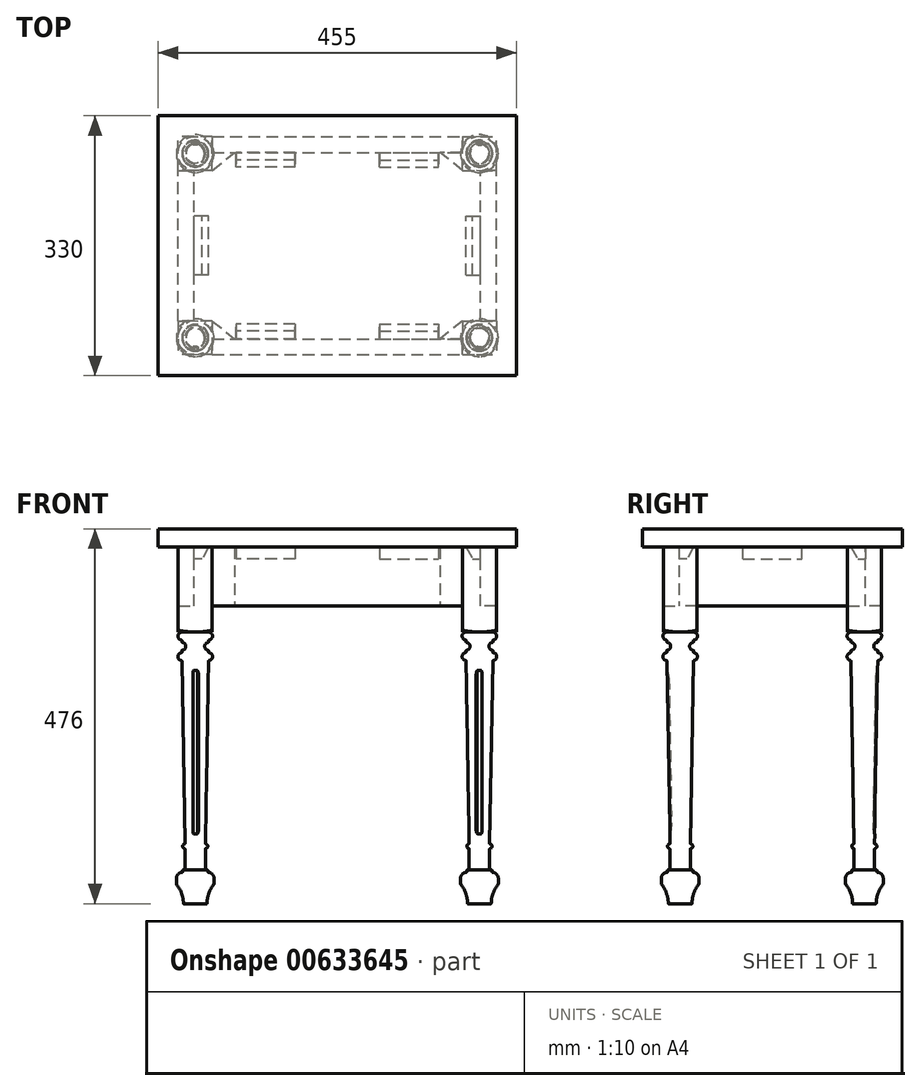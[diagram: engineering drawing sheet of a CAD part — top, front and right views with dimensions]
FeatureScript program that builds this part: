
annotation { "Feature Type Name" : "Feature", "Feature Type Description" : "" }
export const myFeature = defineFeature(function(context is Context, id is Id, definition is map)
    precondition{}
    {
        {
            var Q0;
            Q0=qCreatedBy(makeId("Top.planeOp"),FACE);
            var sketch = newSketch(context, id + "F0", { "sketchPlane" : qUnion([Q0])});
            skLineSegment(sketch, "E0.bottom", {"start": v(-227.5, -165) * mm, "end": v(227.5, -165) * mm});
            skLineSegment(sketch, "E0.top", {"start": v(-227.5, 165) * mm, "end": v(227.5, 165) * mm});
            skLineSegment(sketch, "E0.left", {"start": v(-227.5, -165) * mm, "end": v(-227.5, 165) * mm});
            skLineSegment(sketch, "E0.right", {"start": v(227.5, -165) * mm, "end": v(227.5, 165) * mm});
            skPoint(sketch, "E0.middle", {"position": v(0, 0) * mm});
            skSolve(sketch);
        }
        {
            var Q0;
            Q0 = qSketchRegion(id + "F0", true);
            extrude(context, id + "F1", {"entities" : qUnion([Q0]), "oppositeDirection" : true, "depth" : 23 * mm, "offsetDistance" : 25 * mm});
        }
        {
            var Q0;
            Q0=makeQuery(id+"F1.opExtrude","CAP_FACE",FACE,{"disambiguationData":[OSD([sQuery(id+"F0.wireOp",EDGE,"E0.bottom"),sQuery(id+"F0.wireOp",EDGE,"E0.top"),sQuery(id+"F0.wireOp",EDGE,"E0.left"),sQuery(id+"F0.wireOp",EDGE,"E0.right")])],"isStart":false});
            var sketch = newSketch(context, id + "F2", { "sketchPlane" : qUnion([Q0])});
            skLineSegment(sketch, "E1.bottom", {"start": v(-159, 95.5) * mm, "end": v(-202, 95.5) * mm});
            skLineSegment(sketch, "E1.top", {"start": v(-159, 138.5) * mm, "end": v(-202, 138.5) * mm});
            skLineSegment(sketch, "E1.left", {"start": v(-159, 95.5) * mm, "end": v(-159, 138.5) * mm});
            skLineSegment(sketch, "E1.right", {"start": v(-202, 95.5) * mm, "end": v(-202, 138.5) * mm});
            skPoint(sketch, "E1.middle", {"position": v(-180.5, 117) * mm});
            skSolve(sketch);
        }
        {
            var Q0;
            Q0 = qSketchRegion(id + "F2", true);
            extrude(context, id + "F3", {"entities" : qUnion([Q0]), "depth" : 108 * mm, "offsetDistance" : 25 * mm});
        }
        {
            var Q0;
            Q0=makeQuery(id+"F3.opExtrude","SWEPT_FACE",FACE,{"disambiguationData":[OSD([sQuery(id+"F2.wireOp",EDGE,"E1.right")])]});
            var Q1;
            Q1=makeQuery(id+"F3.opExtrude","SWEPT_FACE",FACE,{"disambiguationData":[OSD([sQuery(id+"F2.wireOp",EDGE,"E1.left")])]});
            cPlane(context, id + "F4", {"entities" : qUnion([Q0, Q1]), "cplaneType" : CPlaneType.MID_PLANE, "offset" : 25 * mm, "width" : 150 * mm, "height" : 150 * mm});
        }
        {
            var Q0;
            Q0=qCreatedBy(id+"F4.planeOp",FACE);
            var sketch = newSketch(context, id + "F5", { "sketchPlane" : qUnion([Q0])});
            skLineSegment(sketch, "E2.0", {"start": v(117, -131) * mm, "end": v(134, -131) * mm});
            skLineSegment(sketch, "E3", {"start": v(117, -131) * mm, "end": v(117, -476) * mm});
            skLineSegment(sketch, "E4", {"start": v(117, -476) * mm, "end": v(132, -476) * mm});
            skArc(sketch, "E5", {"start": v(141, -451) * mm, "mid": v(134.32, -462.71) * mm, "end": v(132, -476) * mm});
            skArc(sketch, "E6", {"start": v(130, -406) * mm, "mid": v(133, -403) * mm, "end": v(130, -400) * mm});
            skLineSegment(sketch, "E7", {"start": v(130, -400) * mm, "end": v(134, -167) * mm});
            skArc(sketch, "E8", {"start": v(134, -167) * mm, "mid": v(139, -162) * mm, "end": v(134, -157) * mm});
            skLineSegment(sketch, "E9", {"start": v(134, -157) * mm, "end": v(134, -154) * mm});
            skArc(sketch, "E10", {"start": v(134, -144) * mm, "mid": v(129, -149) * mm, "end": v(134, -154) * mm});
            skLineSegment(sketch, "E11", {"start": v(134, -144) * mm, "end": v(134, -141) * mm});
            skArc(sketch, "E12", {"start": v(134, -141) * mm, "mid": v(139, -136) * mm, "end": v(134, -131) * mm});
            skLineSegment(sketch, "E13", {"start": v(130, -406) * mm, "end": v(130, -433) * mm});
            skLineSegment(sketch, "E14", {"start": v(130, -433) * mm, "end": v(133, -433) * mm});
            skLineSegment(sketch, "E15", {"start": v(133, -433) * mm, "end": v(133, -436) * mm});
            skLineSegment(sketch, "E16", {"start": v(141, -436) * mm, "end": v(141, -451) * mm});
            skPoint(sketch, "E17.orphan", {"position": v(138.5, -131) * mm});
            skPoint(sketch, "E18.orphan", {"position": v(95.5, -131) * mm});
            skLineSegment(sketch, "E19", {"start": v(133, -436) * mm, "end": v(141, -436) * mm});
            skSolve(sketch);
        }
        {
            var Q0;
            Q0=makeQuery(id+"F5.imprint","IMPRINT",FACE,{"disambiguationData":[TD([[makeQuery(id+"F5.imprint","IMPRINT",EDGE,{"derivedFrom":sQuery(id+"F5.wireOp",EDGE,"E2.0")}),-1.0]])]});
            var Q1;
            Q1=sQuery(id+"F5.wireOp",EDGE,"E3");
            revolve(context, id + "F6", {"operationType" : NewBodyOperationType.ADD, "entities" : qUnion([Q0]), "axis" : qUnion([Q1]), "revolveType" : RevolveType.FULL});
        }
        {
            var Q0;
            Q0=makeQuery(id+"F6.opRevolve","SWEPT_EDGE",EDGE,{"disambiguationData":[OSD([sQuery(id+"F5.wireOp",EDGE,"E16"),sQuery(id+"F5.wireOp",EDGE,"E19")])]});
            fillet(context, id + "F7", {"entities" : qUnion([Q0]), "radius" : 8 * mm, "tangentPropagation" : true, "allowEdgeOverflow" : false});
        }
        {
            var Q0;
            Q0=makeQuery(id+"F6.opRevolve","SWEPT_EDGE",EDGE,{"disambiguationData":[OSD([sQuery(id+"F5.wireOp",EDGE,"E13"),sQuery(id+"F5.wireOp",EDGE,"E14")])]});
            var Q1;
            Q1=makeQuery(id+"F6.opRevolve","SWEPT_EDGE",EDGE,{"disambiguationData":[OSD([sQuery(id+"F5.wireOp",EDGE,"E5"),sQuery(id+"F5.wireOp",EDGE,"E16")])]});
            fillet(context, id + "F8", {"entities" : qUnion([Q0, Q1]), "radius" : 2.5 * mm, "tangentPropagation" : true, "allowEdgeOverflow" : false});
        }
        {
            var Q0;
            Q0=makeQuery(id+"F6.opRevolve","SWEPT_EDGE",EDGE,{"disambiguationData":[OSD([sQuery(id+"F5.wireOp",EDGE,"E14"),sQuery(id+"F5.wireOp",EDGE,"E15")])]});
            var Q1;
            Q1=makeQuery(id+"F7.opFillet","BLEND_EDGE",EDGE,{"blendedFrom":[makeQuery(id+"F6.opRevolve","SWEPT_EDGE",EDGE,{"disambiguationData":[OSD([sQuery(id+"F5.wireOp",EDGE,"E16"),sQuery(id+"F5.wireOp",EDGE,"E19")])]}),makeQuery(id+"F6.opRevolve","SWEPT_FACE",FACE,{"disambiguationData":[OSD([sQuery(id+"F5.wireOp",EDGE,"E15")])]})],"blendedInto":[makeQuery(id+"F6.opRevolve","SWEPT_FACE",FACE,{"disambiguationData":[OSD([sQuery(id+"F5.wireOp",EDGE,"E15")])]})]});
            var Q2;
            Q2=makeQuery(id+"F6.opRevolve","SWEPT_EDGE",EDGE,{"disambiguationData":[OSD([sQuery(id+"F5.wireOp",EDGE,"E6"),sQuery(id+"F5.wireOp",EDGE,"E7")])]});
            var Q3;
            Q3=makeQuery(id+"F6.opRevolve","SWEPT_EDGE",EDGE,{"disambiguationData":[OSD([sQuery(id+"F5.wireOp",EDGE,"E6"),sQuery(id+"F5.wireOp",EDGE,"E13")])]});
            var Q4;
            Q4=makeQuery(id+"F6.opRevolve","SWEPT_EDGE",EDGE,{"disambiguationData":[OSD([sQuery(id+"F5.wireOp",EDGE,"E11"),sQuery(id+"F5.wireOp",EDGE,"E12")])]});
            var Q5;
            Q5=makeQuery(id+"F6.opRevolve","SWEPT_EDGE",EDGE,{"disambiguationData":[OSD([sQuery(id+"F5.wireOp",EDGE,"E10"),sQuery(id+"F5.wireOp",EDGE,"E11")])]});
            var Q6;
            Q6=makeQuery(id+"F6.opRevolve","SWEPT_EDGE",EDGE,{"disambiguationData":[OSD([sQuery(id+"F5.wireOp",EDGE,"E9"),sQuery(id+"F5.wireOp",EDGE,"E10")])]});
            var Q7;
            Q7=makeQuery(id+"F6.opRevolve","SWEPT_EDGE",EDGE,{"disambiguationData":[OSD([sQuery(id+"F5.wireOp",EDGE,"E8"),sQuery(id+"F5.wireOp",EDGE,"E9")])]});
            var Q8;
            Q8=makeQuery(id+"F6.opRevolve","SWEPT_EDGE",EDGE,{"disambiguationData":[OSD([sQuery(id+"F5.wireOp",EDGE,"E7"),sQuery(id+"F5.wireOp",EDGE,"E8")])]});
            var Q9;
            Q9=makeQuery(id+"F6.opRevolve","SWEPT_EDGE",EDGE,{"disambiguationData":[OSD([sQuery(id+"F5.wireOp",EDGE,"E4"),sQuery(id+"F5.wireOp",EDGE,"E5")])]});
            fillet(context, id + "F9", {"entities" : qUnion([Q0, Q1, Q2, Q3, Q4, Q5, Q6, Q7, Q8, Q9]), "radius" : .5 * mm, "tangentPropagation" : true, "allowEdgeOverflow" : false});
        }
        {
            var Q0;
            Q0=makeQuery(id+"F3.opExtrude","SWEPT_EDGE",EDGE,{"disambiguationData":[OSD([sQuery(id+"F2.wireOp",EDGE,"E1.top"),sQuery(id+"F2.wireOp",EDGE,"E1.right")])]});
            var Q1;
            Q1=makeQuery(id+"F3.opExtrude","SWEPT_EDGE",EDGE,{"disambiguationData":[OSD([sQuery(id+"F2.wireOp",EDGE,"E1.bottom"),sQuery(id+"F2.wireOp",EDGE,"E1.left")])]});
            cPlane(context, id + "F10", {"entities" : qUnion([Q0, Q1]), "cplaneType" : CPlaneType.LINE_ANGLE, "offset" : 25 * mm, "angle" : 0 * degree, "width" : 150 * mm, "height" : 150 * mm});
        }
        {
            var Q0;
            Q0=qCreatedBy(id+"F10.planeOp",FACE);
            var sketch = newSketch(context, id + "F11", { "sketchPlane" : qUnion([Q0])});
            skLineSegment(sketch, "E20.0", {"start": v(210.36, -131) * mm, "end": v(210.36, -23) * mm});
            skArc(sketch, "E21", {"start": v(179.69, -128) * mm, "mid": v(186.03, -130.24) * mm, "end": v(192.72, -131) * mm});
            skLineSegment(sketch, "E22", {"start": v(179.69, -128) * mm, "end": v(179.69, -131) * mm});
            skLineSegment(sketch, "E23", {"start": v(179.69, -131) * mm, "end": v(192.72, -131) * mm});
            skSolve(sketch);
        }
        {
            var Q0;
            Q0=makeQuery(id+"F11.imprint","IMPRINT",FACE,{"disambiguationData":[TD([[makeQuery(id+"F11.imprint","IMPRINT",EDGE,{"derivedFrom":sQuery(id+"F11.wireOp",EDGE,"E21")}),-1.0]])]});
            var Q1;
            Q1=sQuery(id+"F11.wireOp",EDGE,"E20.0");
            revolve(context, id + "F12", {"operationType" : NewBodyOperationType.REMOVE, "entities" : qUnion([Q0]), "axis" : qUnion([Q1]), "revolveType" : RevolveType.FULL, "oppositeDirection" : true});
        }
        {
            var Q0;
            Q0=qCreatedBy(id+"F4.planeOp",FACE);
            var sketch = newSketch(context, id + "F13", { "sketchPlane" : qUnion([Q0])});
            skLineSegment(sketch, "E24.0", {"start": v(134, -167.47) * mm, "end": v(100, -167.47) * mm});
            skLineSegment(sketch, "E25.0", {"start": v(104, -399.53) * mm, "end": v(130, -399.53) * mm});
            skLineSegment(sketch, "E26", {"start": v(117, -399.53) * mm, "end": v(117, -167.47) * mm});
            skLineSegment(sketch, "E27", {"start": v(134.02, -165.87) * mm, "end": v(130.21, -387.53) * mm});
            skLineSegment(sketch, "E28", {"start": v(131.12, -189.1) * mm, "end": v(127.88, -377.8) * mm});
            skArc(sketch, "E29", {"start": v(133.79, -179.47) * mm, "mid": v(131.84, -184.12) * mm, "end": v(131.12, -189.1) * mm});
            skArc(sketch, "E30", {"start": v(127.88, -377.8) * mm, "mid": v(128.43, -382.81) * mm, "end": v(130.21, -387.53) * mm});
            skLineSegment(sketch, "E31", {"start": v(147.88, -378.15) * mm, "end": v(151.12, -189.45) * mm, "construction": true});
            skSolve(sketch);
        }
        {
            var Q0;
            Q0=makeQuery(id+"F13.imprint","IMPRINT",FACE,{"disambiguationData":[TD([[makeQuery(id+"F13.imprint","IMPRINT",EDGE,{"derivedFrom":sQuery(id+"F13.wireOp",EDGE,"E28")}),1.0]])]});
            extrude(context, id + "F14", {"entities" : qUnion([Q0]), "operationType" : NewBodyOperationType.REMOVE, "endBound" : BoundingType.SYMMETRIC, "oppositeDirection" : true, "depth" : 6 * mm, "offsetDistance" : 25 * mm});
        }
        {
            var Q0;
            Q0=makeQuery(id+"F14.boolean.opBoolean","COPY",EDGE,{"derivedFrom":makeQuery(id+"F14.opExtrude","CAP_EDGE",EDGE,{"disambiguationData":[OSD([sQuery(id+"F13.wireOp",EDGE,"E28")])],"isStart":false})});
            var Q1;
            Q1=makeQuery(id+"F14.boolean.opBoolean","COPY",EDGE,{"derivedFrom":makeQuery(id+"F14.opExtrude","CAP_EDGE",EDGE,{"disambiguationData":[OSD([sQuery(id+"F13.wireOp",EDGE,"E28")])],"isStart":true})});
            var Q2;
            Q2=makeQuery(id+"F14.boolean.opBoolean","INTERSECT",EDGE,{"derivedFrom":[makeQuery(id+"F6.opRevolve","SWEPT_FACE",FACE,{"disambiguationData":[OSD([sQuery(id+"F5.wireOp",EDGE,"E7")])]}),makeQuery(id+"F14.opExtrude","CAP_FACE",FACE,{"disambiguationData":[OSD([sQuery(id+"F13.wireOp",EDGE,"E27"),sQuery(id+"F13.wireOp",EDGE,"E28"),sQuery(id+"F13.wireOp",EDGE,"E29"),sQuery(id+"F13.wireOp",EDGE,"E30")])],"isStart":false})]});
            fillet(context, id + "F15", {"entities" : qUnion([Q0, Q1, Q2]), "radius" : .9 * mm, "tangentPropagation" : true, "allowEdgeOverflow" : false});
        }
        {
            var Q0;
            Q0=makeQuery(id+"F3.opExtrude","SWEPT_BODY",BODY,{"disambiguationData":[OSD([sQuery(id+"F2.wireOp",EDGE,"E1.bottom"),sQuery(id+"F2.wireOp",EDGE,"E1.top"),sQuery(id+"F2.wireOp",EDGE,"E1.left"),sQuery(id+"F2.wireOp",EDGE,"E1.right")])]});
            var Q1;
            Q1=qCreatedBy(makeId("Right.planeOp"),FACE);
            mirror(context, id + "F16", {"entities" : qUnion([Q0]), "mirrorPlane" : qUnion([Q1])});
        }
        {
            var Q0;
            Q0=makeQuery(id+"F1.opExtrude","CAP_FACE",FACE,{"disambiguationData":[OSD([sQuery(id+"F0.wireOp",EDGE,"E0.bottom"),sQuery(id+"F0.wireOp",EDGE,"E0.top"),sQuery(id+"F0.wireOp",EDGE,"E0.left"),sQuery(id+"F0.wireOp",EDGE,"E0.right")])],"isStart":false});
            var sketch = newSketch(context, id + "F17", { "sketchPlane" : qUnion([Q0])});
            skPoint(sketch, "E32.0", {"position": v(-159, 138.5) * mm});
            skPoint(sketch, "E33.0", {"position": v(159, 138.5) * mm});
            skLineSegment(sketch, "E34.bottom", {"start": v(-159, 138.5) * mm, "end": v(159, 138.5) * mm});
            skLineSegment(sketch, "E34.top", {"start": v(-159, 118.5) * mm, "end": v(159, 118.5) * mm});
            skLineSegment(sketch, "E34.left", {"start": v(-159, 138.5) * mm, "end": v(-159, 118.5) * mm});
            skLineSegment(sketch, "E34.right", {"start": v(159, 138.5) * mm, "end": v(159, 118.5) * mm});
            skSolve(sketch);
        }
        {
            var Q0;
            Q0 = qSketchRegion(id + "F17", true);
            extrude(context, id + "F18", {"entities" : qUnion([Q0]), "depth" : 75 * mm, "offsetDistance" : 25 * mm});
        }
        {
            var Q0;
            Q0=makeQuery(id+"F3.opExtrude","SWEPT_BODY",BODY,{"disambiguationData":[OSD([sQuery(id+"F2.wireOp",EDGE,"E1.bottom"),sQuery(id+"F2.wireOp",EDGE,"E1.top"),sQuery(id+"F2.wireOp",EDGE,"E1.left"),sQuery(id+"F2.wireOp",EDGE,"E1.right")])]});
            var Q1;
            Q1=makeQuery(id+"F18.opExtrude","SWEPT_BODY",BODY,{"disambiguationData":[OSD([sQuery(id+"F17.wireOp",EDGE,"E34.bottom"),sQuery(id+"F17.wireOp",EDGE,"E34.top"),sQuery(id+"F17.wireOp",EDGE,"E34.left"),sQuery(id+"F17.wireOp",EDGE,"E34.right")])]});
            var Q2;
            Q2=makeQuery(id+"F16.opPattern","COPY",BODY,{"derivedFrom":makeQuery(id+"F3.opExtrude","SWEPT_BODY",BODY,{"disambiguationData":[OSD([sQuery(id+"F2.wireOp",EDGE,"E1.bottom"),sQuery(id+"F2.wireOp",EDGE,"E1.top"),sQuery(id+"F2.wireOp",EDGE,"E1.left"),sQuery(id+"F2.wireOp",EDGE,"E1.right")])]}),"instanceName":"1"});
            var Q3;
            Q3=qCreatedBy(makeId("Front.planeOp"),FACE);
            mirror(context, id + "F19", {"entities" : qUnion([Q0, Q1, Q2]), "mirrorPlane" : qUnion([Q3])});
        }
        {
            var Q0;
            Q0=makeQuery(id+"F1.opExtrude","CAP_FACE",FACE,{"disambiguationData":[OSD([sQuery(id+"F0.wireOp",EDGE,"E0.bottom"),sQuery(id+"F0.wireOp",EDGE,"E0.top"),sQuery(id+"F0.wireOp",EDGE,"E0.left"),sQuery(id+"F0.wireOp",EDGE,"E0.right")])],"isStart":false});
            var sketch = newSketch(context, id + "F20", { "sketchPlane" : qUnion([Q0])});
            skPoint(sketch, "E35.0", {"position": v(202, 95.5) * mm});
            skPoint(sketch, "E36.0", {"position": v(159, -95.5) * mm});
            skLineSegment(sketch, "E37.bottom", {"start": v(202, 95.5) * mm, "end": v(182, 95.5) * mm});
            skLineSegment(sketch, "E37.top", {"start": v(202, -95.5) * mm, "end": v(182, -95.5) * mm});
            skLineSegment(sketch, "E37.left", {"start": v(202, 95.5) * mm, "end": v(202, -95.5) * mm});
            skLineSegment(sketch, "E37.right", {"start": v(182, 95.5) * mm, "end": v(182, -95.5) * mm});
            skSolve(sketch);
        }
        {
            var Q0;
            Q0 = qSketchRegion(id + "F20", true);
            var Q1;
            Q1=makeQuery(id+"F19.opPattern","COPY",FACE,{"derivedFrom":makeQuery(id+"F18.opExtrude","CAP_FACE",FACE,{"disambiguationData":[OSD([sQuery(id+"F17.wireOp",EDGE,"E34.bottom"),sQuery(id+"F17.wireOp",EDGE,"E34.top"),sQuery(id+"F17.wireOp",EDGE,"E34.left"),sQuery(id+"F17.wireOp",EDGE,"E34.right")])],"isStart":false}),"instanceName":"1"});
            extrude(context, id + "F21", {"entities" : qUnion([Q0]), "endBound" : BoundingType.UP_TO_SURFACE, "depth" : 25 * mm, "endBoundEntityFace" : qUnion([Q1]), "offsetDistance" : 25 * mm});
        }
        {
            var Q0;
            Q0=makeQuery(id+"F21.opExtrude","SWEPT_BODY",BODY,{"disambiguationData":[OSD([sQuery(id+"F20.wireOp",EDGE,"E37.bottom"),sQuery(id+"F20.wireOp",EDGE,"E37.top"),sQuery(id+"F20.wireOp",EDGE,"E37.left"),sQuery(id+"F20.wireOp",EDGE,"E37.right")])]});
            var Q1;
            Q1=qCreatedBy(makeId("Right.planeOp"),FACE);
            mirror(context, id + "F22", {"entities" : qUnion([Q0]), "mirrorPlane" : qUnion([Q1])});
        }
        {
            var Q0;
            Q0=makeQuery(id+"F19.opPattern","COPY",FACE,{"derivedFrom":makeQuery(id+"F18.opExtrude","CAP_FACE",FACE,{"disambiguationData":[OSD([sQuery(id+"F17.wireOp",EDGE,"E34.bottom"),sQuery(id+"F17.wireOp",EDGE,"E34.top"),sQuery(id+"F17.wireOp",EDGE,"E34.left"),sQuery(id+"F17.wireOp",EDGE,"E34.right")])],"isStart":false}),"instanceName":"1"});
            var sketch = newSketch(context, id + "F23", { "sketchPlane" : qUnion([Q0])});
            skFitSpline(sketch, "E38.0", {"points": [v(-159, -95.5) * mm, v(-159, -109.83) * mm, v(-159, -124.17) * mm, v(-159, -138.5) * mm]});
            skLineSegment(sketch, "E39", {"start": v(-159, -95.5) * mm, "end": v(-130.6, -118.5) * mm});
            skLineSegment(sketch, "E40", {"start": v(-130.6, -118.5) * mm, "end": v(-159, -118.5) * mm});
            skPoint(sketch, "E41.orphan", {"position": v(-159, -138.5) * mm});
            skSolve(sketch);
        }
        {
            var Q0;
            Q0=makeQuery(id+"F23.imprint","IMPRINT",FACE,{"disambiguationData":[TD([[makeQuery(id+"F23.imprint","IMPRINT",EDGE,{"derivedFrom":sQuery(id+"F23.wireOp",EDGE,"E38.0")}),1.0]])]});
            var Q1;
            Q1=makeQuery(id+"F1.opExtrude","CAP_FACE",FACE,{"disambiguationData":[OSD([sQuery(id+"F0.wireOp",EDGE,"E0.bottom"),sQuery(id+"F0.wireOp",EDGE,"E0.top"),sQuery(id+"F0.wireOp",EDGE,"E0.left"),sQuery(id+"F0.wireOp",EDGE,"E0.right")])],"isStart":false});
            extrude(context, id + "F24", {"entities" : qUnion([Q0]), "endBound" : BoundingType.UP_TO_SURFACE, "oppositeDirection" : true, "depth" : 25 * mm, "endBoundEntityFace" : qUnion([Q1]), "offsetDistance" : 25 * mm});
        }
        {
            var Q0;
            Q0=makeQuery(id+"F24.opExtrude","SWEPT_BODY",BODY,{"disambiguationData":[OSD([sQuery(id+"F23.wireOp",EDGE,"E38.0"),sQuery(id+"F23.wireOp",EDGE,"E39"),sQuery(id+"F23.wireOp",EDGE,"E40")])]});
            var Q1;
            Q1=qCreatedBy(makeId("Right.planeOp"),FACE);
            mirror(context, id + "F25", {"entities" : qUnion([Q0]), "mirrorPlane" : qUnion([Q1])});
        }
        {
            var Q0;
            Q0=makeQuery(id+"F24.opExtrude","SWEPT_BODY",BODY,{"disambiguationData":[OSD([sQuery(id+"F23.wireOp",EDGE,"E38.0"),sQuery(id+"F23.wireOp",EDGE,"E39"),sQuery(id+"F23.wireOp",EDGE,"E40")])]});
            var Q1;
            Q1=makeQuery(id+"F25.opPattern","COPY",BODY,{"derivedFrom":makeQuery(id+"F24.opExtrude","SWEPT_BODY",BODY,{"disambiguationData":[OSD([sQuery(id+"F23.wireOp",EDGE,"E38.0"),sQuery(id+"F23.wireOp",EDGE,"E39"),sQuery(id+"F23.wireOp",EDGE,"E40")])]}),"instanceName":"1"});
            var Q2;
            Q2=qCreatedBy(makeId("Front.planeOp"),FACE);
            mirror(context, id + "F26", {"entities" : qUnion([Q0, Q1]), "mirrorPlane" : qUnion([Q2])});
        }
        {
            var Q0;
            Q0=qCreatedBy(makeId("Front.planeOp"),FACE);
            var sketch = newSketch(context, id + "F27", { "sketchPlane" : qUnion([Q0])});
            skLineSegment(sketch, "E42.0", {"start": v(-182, -38) * mm, "end": v(-182, -23) * mm});
            skLineSegment(sketch, "E43", {"start": v(-163.34, -23) * mm, "end": v(-182, -23) * mm});
            skPoint(sketch, "E44.orphan", {"position": v(-182, -98) * mm});
            skLineSegment(sketch, "E45", {"start": v(-163.34, -23) * mm, "end": v(-172, -38) * mm});
            skLineSegment(sketch, "E46", {"start": v(-172, -38) * mm, "end": v(-182, -38) * mm});
            skSolve(sketch);
        }
        {
            var Q0;
            Q0 = qSketchRegion(id + "F27", true);
            extrude(context, id + "F28", {"entities" : qUnion([Q0]), "endBound" : BoundingType.SYMMETRIC, "depth" : 75 * mm, "offsetDistance" : 25 * mm});
        }
        {
            var Q0;
            Q0=makeQuery(id+"F22.opPattern","COPY",FACE,{"derivedFrom":makeQuery(id+"F21.opExtrude","SWEPT_FACE",FACE,{"disambiguationData":[OSD([sQuery(id+"F20.wireOp",EDGE,"E37.right")])]}),"instanceName":"1"});
            var Q1;
            Q1=qCreatedBy(makeId("Right.planeOp"),FACE);
            cPlane(context, id + "F29", {"entities" : qUnion([Q0, Q1]), "cplaneType" : CPlaneType.MID_PLANE, "offset" : 170 * mm, "oppositeDirection" : true, "width" : 150 * mm, "height" : 150 * mm});
        }
        {
            var Q0;
            Q0=qCreatedBy(id+"F29.planeOp",FACE);
            var sketch = newSketch(context, id + "F30", { "sketchPlane" : qUnion([Q0])});
            skLineSegment(sketch, "E47.0", {"start": v(118.5, -23) * mm, "end": v(118.5, -38) * mm});
            skLineSegment(sketch, "E48", {"start": v(118.5, -23) * mm, "end": v(99.84, -23) * mm});
            skLineSegment(sketch, "E49", {"start": v(99.84, -23) * mm, "end": v(108.5, -38) * mm});
            skLineSegment(sketch, "E50", {"start": v(108.5, -38) * mm, "end": v(118.5, -38) * mm});
            skPoint(sketch, "E51.orphan", {"position": v(118.5, -98) * mm});
            skSolve(sketch);
        }
        {
            var Q0;
            Q0=makeQuery(id+"F30.imprint","IMPRINT",FACE,{"disambiguationData":[TD([[makeQuery(id+"F30.imprint","IMPRINT",EDGE,{"derivedFrom":sQuery(id+"F30.wireOp",EDGE,"E47.0")}),-1.0]])]});
            extrude(context, id + "F31", {"entities" : qUnion([Q0]), "endBound" : BoundingType.SYMMETRIC, "depth" : 75 * mm, "offsetDistance" : 25 * mm});
        }
        {
            var Q0;
            Q0=makeQuery(id+"F31.opExtrude","SWEPT_BODY",BODY,{"disambiguationData":[OSD([sQuery(id+"F30.wireOp",EDGE,"E47.0"),sQuery(id+"F30.wireOp",EDGE,"E48"),sQuery(id+"F30.wireOp",EDGE,"E49"),sQuery(id+"F30.wireOp",EDGE,"E50")])]});
            var Q1;
            Q1=qCreatedBy(makeId("Front.planeOp"),FACE);
            mirror(context, id + "F32", {"entities" : qUnion([Q0]), "mirrorPlane" : qUnion([Q1])});
        }
        {
            var Q0;
            Q0=makeQuery(id+"F31.opExtrude","SWEPT_BODY",BODY,{"disambiguationData":[OSD([sQuery(id+"F30.wireOp",EDGE,"E47.0"),sQuery(id+"F30.wireOp",EDGE,"E48"),sQuery(id+"F30.wireOp",EDGE,"E49"),sQuery(id+"F30.wireOp",EDGE,"E50")])]});
            var Q1;
            Q1=makeQuery(id+"F28.opExtrude","SWEPT_BODY",BODY,{"disambiguationData":[OSD([sQuery(id+"F27.wireOp",EDGE,"E42.0"),sQuery(id+"F27.wireOp",EDGE,"E43"),sQuery(id+"F27.wireOp",EDGE,"E45"),sQuery(id+"F27.wireOp",EDGE,"E46")])]});
            var Q2;
            Q2=makeQuery(id+"F32.opPattern","COPY",BODY,{"derivedFrom":makeQuery(id+"F31.opExtrude","SWEPT_BODY",BODY,{"disambiguationData":[OSD([sQuery(id+"F30.wireOp",EDGE,"E47.0"),sQuery(id+"F30.wireOp",EDGE,"E48"),sQuery(id+"F30.wireOp",EDGE,"E49"),sQuery(id+"F30.wireOp",EDGE,"E50")])]}),"instanceName":"1"});
            var Q3;
            Q3=qCreatedBy(makeId("Right.planeOp"),FACE);
            mirror(context, id + "F33", {"entities" : qUnion([Q0, Q1, Q2]), "mirrorPlane" : qUnion([Q3])});
        }
    });
